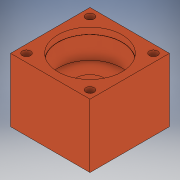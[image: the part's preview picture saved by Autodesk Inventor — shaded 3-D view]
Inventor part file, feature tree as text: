
AUTODESK INVENTOR PART (.ipt)
format: ipt  version: 2018 (Build 220112000, 112)  size: 145,920 bytes
history: native  units: in
note: dims shown in document units (in); Inventor stores cm internally (conversion verified against a paired STEP export)
features: sketch x7, extrude x5, hole x2
ambient origin geometry x8: Origin, YZ Plane, XZ Plane, XY Plane, X Axis, Y Axis, Z Axis, Center Point
bodies: Solid1 (feature_tree)
feature tree (14):
  extrude  "Extrusion1"  Depth=1.25in
  hole  "Hole1"  [1 undecoded]
  extrude  "Extrusion2"  Depth=0.45in
  extrude  "Extrusion3"  Depth=0.502in TaperAngle=0.0deg
  hole  "Hole2"  [1 undecoded]
  sketch  "Sketch1"  dims[d0=1.25in d1=1.25in]
  sketch  "Sketch2"  dims[d2=1.0in d3=0.0in]
  sketch  "Sketch3"  dims[d4=0.4531in d5=0.75in d6=0.375in d7=0.25in d8=0.5635in d9=1.0in d10=0.8108in d11=1.004in]
  sketch  "Sketch4"  dims[d12=0.45in d13=0.0in d14=1.01in]
  sketch  "Sketch7"  dims[d26=1.0in d27=0.13in d28=0.328in d29=0.375in d30=0.25in d31=0.5635in d32=0.484in d33=0.8108in]
  sketch  "Sketch5"  dims[d15=0.1in d16=0.0in d17=0.502in d19=0.0in d20=0.45in]
  sketch  "Sketch6"  dims[d21=0.51in d23=0.0in d24=0.1in d25=1.0in]
  extrude  "Extrusion4"  [1 undecoded]
  extrude  "Extrusion5"  [1 undecoded]
note: 4 required parameter values undecoded (feature->parameter linkage not recoverable at this tier; creation-order binding heuristic only, values carry confidence <= 0.55)
